# Revit family: Hager-Orion-IP65-D160-Cl.I-Steel_encl-630A-PT-pt
name_source: partatom
category: Equipement électrique
units: mm (PartAtom-declared; Revit-internal decimal feet)

## family parameters
Configuration du panneau = Deux colonnes, circuits au sein
Cote de connecteur circulaire = Utiliser le diamètre
Couper avec des vides une fois chargée = Non
Hôte = Face
Partagée = Non
Point de calcul de pièce = Non
Type d'élément = Tableau de raccordement

## types (3) — shared parameters
Commentaires du type = Orion
EF000003 - Método de montagem = EV000384 - Montagem em superfície (gesso)
EF000007 - Cor = EV000270 - Cinzento
EF000049 - Profundidade = 160 mm  [stored 0.524934 ft]
EF000116 - Número RAL = 7035
EF000118 - Com tampa de montagem = Oui
EF000339 - Tipo de difusor = EV004216 - Porta
EF001088 - Extensão possível = Non
EF001131 - Profundidade interior = 160 mm  [stored 0.524934 ft]
EF001596 - Material do corpo = EV000179 - Aço
EF003532 - Adequado para uso no exterior = Non
EF004293 - Força de impacto = EV008784 - IK10
EF004464 - Tipo de porta = EV002646 - Único
EF005474 - Grau de proteção (IP) = EV006421 - IP65
EF006244 - Tampa/porta transparente = Non
EF006306 - Com fecho = Oui
EF007800 - Adequado para proteção contra raios = Non
EF008873 - Corrente nominal (In) = 630 A
EF009170 - Espessura do material do invólucro = 2 mm  [stored 0.00656168 ft]
EF009171 - Espessura do material da porta/tampa = 2 mm  [stored 0.00656168 ft]
EF009212 - Tipo de tampa = EV009916 - Com recuo
EF015940 - Tampa com libertação de sobrepressão = Non
Fabricant = Hager
HG000002 - Com porta ou tampa = Oui
HG000003 - Gama = Orion
HG000006 - Encastrado = Non
HG000009 - Porta dupla = Non
HG000010 - Portas assimétricas = Non
HG000023 - Recinto de secção dupla = Non
HG000024 - Altura da secção inferior = 800 mm
HG000026 - Instalação no chão = Non
zero-valued in all types: EF000218 - Profundidade incorporada, EF002950 - Largura em número de módulos, EF004427 - Número de módulos, Elévation par défaut, HG000027 - Altura da Plinta

## per-type parameters (varying)
| type | EF000008 - Largura | EF000040 - Altura | EF000266 - Número de linhas | EF000437 - Número de entradas de condutores | EF009554 - Número de aberturas para placas de flange | HG000004 - Referência do Fabricante |
| Montagem em superfície (gesso) IP65 L200 A250 P160  - FL701L | 200 mm  [stored 0.656168 ft] | 250 mm  [stored 0.82021 ft] | 0 | 2 | 2 | FL701L |
| Montagem em superfície (gesso) IP65 L250 A300 P160  - FL702L | 250 mm  [stored 0.82021 ft] | 300 mm  [stored 0.984252 ft] | 1 | 1 | 1 | FL702L |
| Montagem em superfície (gesso) IP65 L300 A300 P160  - FL703L | 300 mm  [stored 0.984252 ft] | 300 mm  [stored 0.984252 ft] | 0 | 2 | 2 | FL703L |

note: [stored X ft] marks values corroborated as IEEE doubles in the binary element streams (Revit-internal decimal feet)

## geometry (parser evidence)
native form markers: Sweep x6
no freeform markers — native parametric forms only
